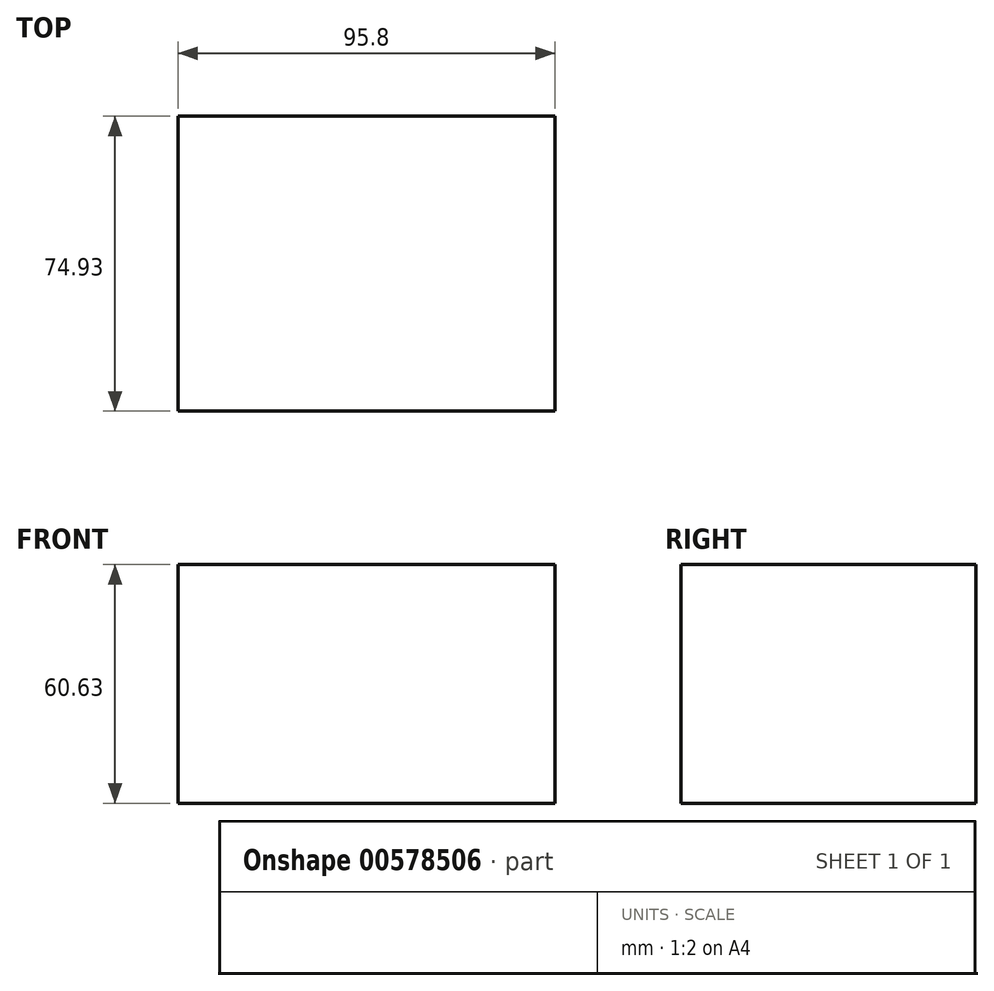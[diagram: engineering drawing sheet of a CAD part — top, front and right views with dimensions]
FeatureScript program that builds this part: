
annotation { "Feature Type Name" : "Feature", "Feature Type Description" : "" }
export const myFeature = defineFeature(function(context is Context, id is Id, definition is map)
    precondition{}
    {
        {
            var Q0;
            Q0=qCreatedBy(makeId("Front.planeOp"),FACE);
            var sketch = newSketch(context, id + "F0", { "sketchPlane" : qUnion([Q0])});
            skLineSegment(sketch, "E0.bottom", {"start": v(-58.6, 41.48) * mm, "end": v(37.21, 41.48) * mm});
            skLineSegment(sketch, "E0.top", {"start": v(-58.6, -19.15) * mm, "end": v(37.21, -19.15) * mm});
            skLineSegment(sketch, "E0.left", {"start": v(-58.6, 41.48) * mm, "end": v(-58.6, -19.15) * mm});
            skLineSegment(sketch, "E0.right", {"start": v(37.21, 41.48) * mm, "end": v(37.21, -19.15) * mm});
            skSolve(sketch);
        }
        {
            var Q0;
            Q0 = qSketchRegion(id + "F0", true);
            extrude(context, id + "F1", {"entities" : qUnion([Q0]), "depth" : 74.93 * mm, "offsetDistance" : 25.4 * mm});
        }
    });
